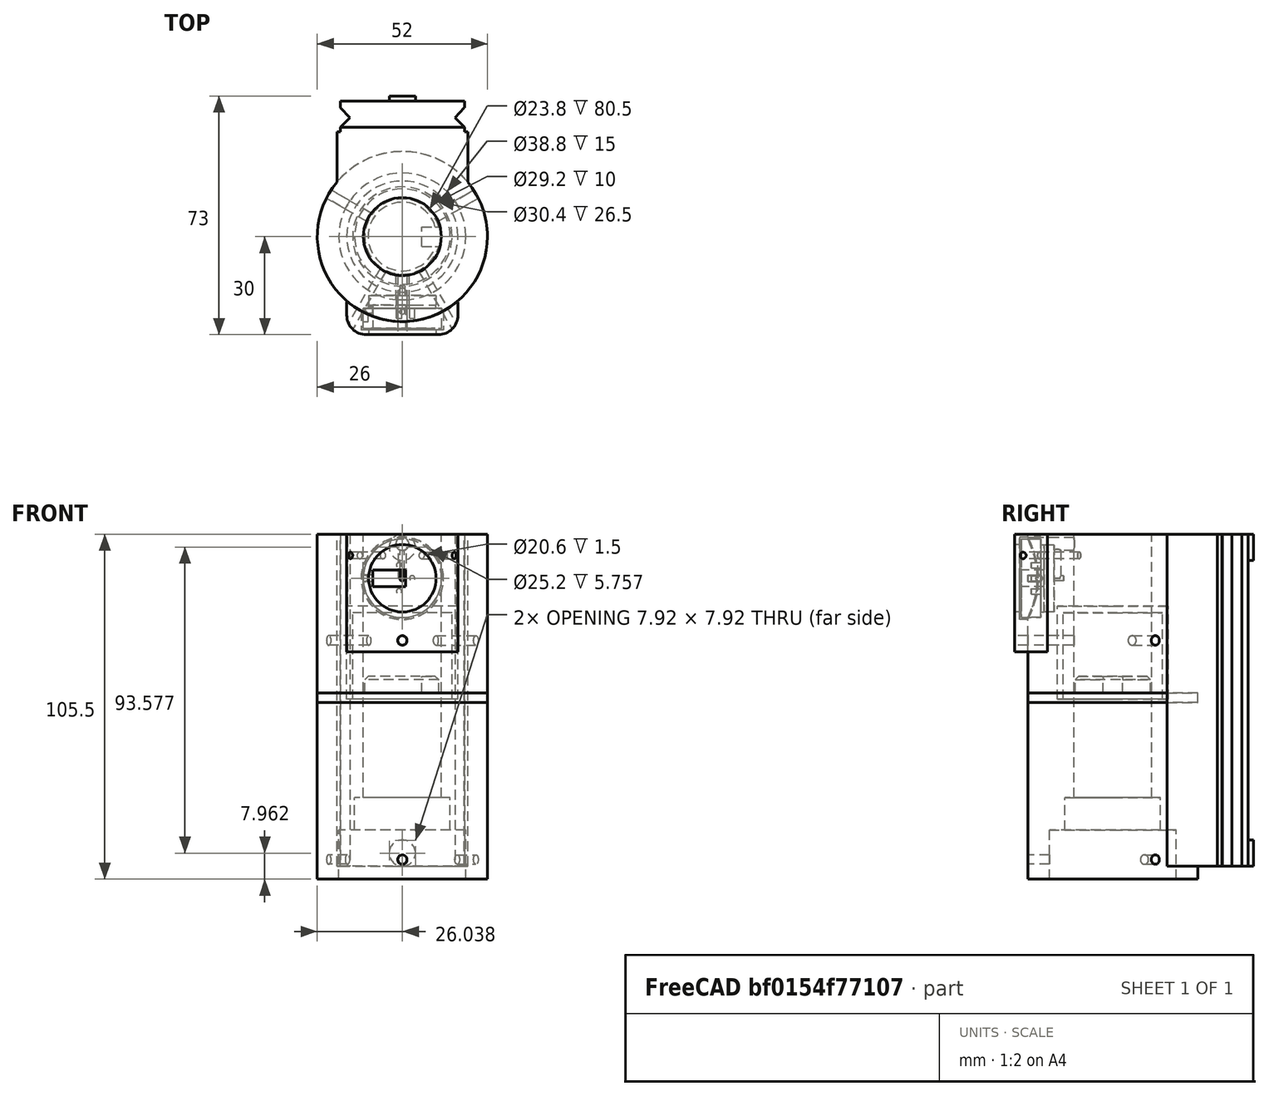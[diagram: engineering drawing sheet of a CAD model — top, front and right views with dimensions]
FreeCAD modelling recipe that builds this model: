
FCSTD DOCUMENT  (FreeCAD 0.17R13387 (Git))
Label: polar scope
License: All rights reserved
LicenseURL: http://en.wikipedia.org/wiki/All_rights_reserved
objects: Part::Cylinder×31, Part::MultiFuse×15, Part::Cut×11, Part::Feature×10, Part::Box×8, Part::Chamfer×2, Part::Fillet×1, App::Part×1
note: 78 computed .brp shape members not serialized (recipe doc carries the construction recipe); baked Part::Feature solids carry a one-line shape summary decoded from their .brp

FEATURE [Part::Feature] Chamfer008019  label="Zaklad009"
  shape: bbox 61 x 63.5 x 101.5 mm, 101 faces (baked)
FEATURE [Part::Cylinder] Cylinder014005804  label="Válec717"
  Angle = 360
  AttacherType = Attacher::AttachEngine3D
  Height = 25
  Placement = pos=(0,0,-51) rot=(0,0,1;0rad)
  Radius = 14.6
FEATURE [Part::Cylinder] Cylinder014005805  label="Válec718"
  Angle = 360
  AttacherType = Attacher::AttachEngine3D
  Height = 40
  Placement = pos=(-40,1,-17.5) rot=(0,1,0;1.5708rad)
  Radius = 0.01
FEATURE [Part::Box] Box207  label="Krychle182"
  AttacherType = Attacher::AttachEngine3D
  Height = 13
  Length = 0.01
  Placement = pos=(-32,-4.5,-55) rot=(0,0,1;0rad)
  Width = 28
FEATURE [Part::Cylinder] Cylinder014005807  label="Válec720"
  Angle = 360
  AttacherType = Attacher::AttachEngine3D
  Height = 74
  Placement = pos=(-40,0,-46.5) rot=(0,1,0;1.5708rad)
  Radius = 0.01
FEATURE [Part::Cylinder] Cylinder014005808  label="Válec721"
  Angle = 360
  AttacherType = Attacher::AttachEngine3D
  Height = 40
  Placement = pos=(-40,16,-17.5) rot=(0,1,0;1.5708rad)
  Radius = 0.01
FEATURE [Part::Box] Box205  label="Krychle180"
  AttacherType = Attacher::AttachEngine3D
  Height = 101.5
  Length = 51
  Placement = pos=(-25.5,-22.5,-51) rot=(0,0,1;0rad)
  Width = 44
FEATURE [Part::Chamfer] Chamfer008018
  Base = -> Box205
  Edges = 2 edges r=7: [Edge1,Edge5]
FEATURE [Part::Box] Box206  label="Krychle181"
  AttacherType = Attacher::AttachEngine3D
  Height = 13
  Length = 0.01
  Placement = pos=(30,-4.5,-55) rot=(0,0,1;0rad)
  Width = 28
FEATURE [Part::Cylinder] Cylinder014005806  label="Válec719"
  Angle = 360
  AttacherType = Attacher::AttachEngine3D
  Height = 74
  Placement = pos=(-40,19,-46.5) rot=(0,1,0;1.5708rad)
  Radius = 0.01
FEATURE [Part::Cylinder] Cylinder014005809  label="Válec722"
  Angle = 360
  AttacherType = Attacher::AttachEngine3D
  Height = 105.5
  Placement = pos=(0,0,-51) rot=(0,0,1;0rad)
  Radius = 11.9
FEATURE [Part::MultiFuse] Fusion001089083
  Shapes = -> [Box206,Box207]
FEATURE [Part::MultiFuse] Fusion001089082
  Shapes = -> [Cylinder014005807,Cylinder014005806]
FEATURE [Part::MultiFuse] Fusion001089078
  Shapes = -> [Fusion001089083,Fusion001089082]
FEATURE [Part::Cut] Cut061098124  label="Zaklad 004"
  Base = -> Chamfer008019
  Tool = -> Fusion001089078
FEATURE [Part::MultiFuse] Fusion001089079
  Shapes = -> [Cylinder014005805,Cylinder014005808]
FEATURE [Part::Cut] Cut061098123  label="RA Zaklad004"
  Base = -> Cut061098124
  Tool = -> Fusion001089079
FEATURE [Part::MultiFuse] Fusion001089081  label="BASE"
  Shapes = -> [Cut061098123,Chamfer008018]
FEATURE [Part::Cylinder] Cylinder014005812  label="Válec725"
  Angle = 360
  AttacherType = Attacher::AttachEngine3D
  Height = 15
  Placement = pos=(0,0,-51) rot=(0,0,1;0rad)
  Radius = 19.4
FEATURE [Part::Cylinder] Cylinder014005813  label="Válec726"
  Angle = 360
  AttacherType = Attacher::AttachEngine3D
  Height = 105.5
  Placement = pos=(0,0,-55) rot=(1,0,0;0rad)
  Radius = 26
FEATURE [Part::Box] Box  label="Krychle"
  AttacherType = Attacher::AttachEngine3D
  Height = 101.5
  Length = 64
  Placement = pos=(-32,-32,-51) rot=(0,0,1;0rad)
  Width = 64
FEATURE [Part::Cut] Cut
  Base = -> Fusion001089081
  Tool = -> Box
FEATURE [Part::Box] Box208  label="Krychle183"
  AttacherType = Attacher::AttachEngine3D
  Height = 101.5
  Length = 40
  Placement = pos=(-20,0,-51) rot=(0,0,1;0rad)
  Width = 32
FEATURE [Part::MultiFuse] Fusion
  Shapes = -> [Cylinder014005813,Box208]
FEATURE [Part::MultiFuse] Fusion001089080
  Placement = pos=(0,0,-4) rot=(0,0,1;0rad)
  Shapes = -> [Cylinder014005809,Cylinder014005804,Cylinder014005812]
FEATURE [Part::MultiFuse] Fusion001089084
  Shapes = -> [Cut,Fusion]
FEATURE [Part::Cut] Cut061098125
  Base = -> Fusion001089084
  Tool = -> Fusion001089080
FEATURE [Part::Cylinder] Cylinder  label="bat1"
  Angle = 360
  AttacherType = Attacher::AttachEngine3D
  Height = 8
  Placement = pos=(0,-18,37) rot=(1,0,0;1.5708rad)
  Radius = 10.3
FEATURE [Part::Cylinder] Cylinder014005814  label="Válec727"
  Angle = 360
  AttacherType = Attacher::AttachEngine3D
  Height = 31
  Placement = pos=(0,0,-49) rot=(1,0,0;1.5708rad)
  Radius = 1.44
FEATURE [Part::Feature] Cylinder014005814001  label="Válec728"
  Placement = pos=(0,0,0) rot=(0,0,1;2.0944rad)
  shape: bbox 28.29 x 17.99 x 2.88 mm, 3 faces (baked)
FEATURE [Part::Feature] Cylinder014005814002  label="Válec729"
  Placement = pos=(0,0,0) rot=(0,0,1;4.18879rad)
  shape: bbox 28.29 x 17.99 x 2.88 mm, 3 faces (baked)
FEATURE [Part::Cylinder] Cylinder014005814003  label="led"
  Angle = 360
  AttacherType = Attacher::AttachEngine3D
  Height = 15
  Placement = pos=(0,-11,47.5) rot=(1,0,0;1.5708rad)
  Radius = 2
FEATURE [Part::Cylinder] Cylinder014005814004  label="Válec731"
  Angle = 360
  AttacherType = Attacher::AttachEngine3D
  Height = 31
  Placement = pos=(0,0,18) rot=(1,0,0;1.5708rad)
  Radius = 1.44
FEATURE [Part::Cylinder] Cylinder014005814005  label="bat2"
  Angle = 360
  AttacherType = Attacher::AttachEngine3D
  Height = 4
  Placement = pos=(0,-22,37) rot=(1,0,0;1.5708rad)
  Radius = 12
FEATURE [Part::Feature] Cylinder014005814004001  label="Válec732"
  Placement = pos=(0,0,0) rot=(0,0,1;2.0944rad)
  shape: bbox 28.29 x 17.99 x 2.88 mm, 3 faces (baked)
FEATURE [Part::Feature] Cylinder014005814004002  label="Válec733"
  Placement = pos=(0,0,0) rot=(0,0,1;4.18879rad)
  shape: bbox 28.29 x 17.99 x 2.88 mm, 3 faces (baked)
FEATURE [Part::Cylinder] Cylinder014005814004003  label="bat003"
  Angle = 360
  AttacherType = Attacher::AttachEngine3D
  Height = 3
  Placement = pos=(0,-15,37) rot=(1,0,0;1.5708rad)
  Radius = 0.8
FEATURE [Part::Cylinder] Cylinder014005814004004  label="Válec"
  Angle = 360
  AttacherType = Attacher::AttachEngine3D
  Height = 11
  Placement = pos=(0,-17,37) rot=(0,0,1;0rad)
  Radius = 1.2
FEATURE [Part::Cylinder] Cylinder014005814004005  label="Válec734"
  Angle = 360
  AttacherType = Attacher::AttachEngine3D
  Height = 2
  Placement = pos=(0,-23,48) rot=(0,0,1;0rad)
  Radius = 0.8
FEATURE [Part::MultiFuse] Fusion001089085
  Shapes = -> [Cylinder,Cylinder014005814,Cylinder014005814001,Cylinder014005814002,Cylinder014005814003,Cylinder014005814004,Cylinder014005814005,Cylinder014005814004001,Cylinder014005814004002,Cylinder014005814004003,Cylinder014005814004004,Cylinder014005814004005]
FEATURE [Part::Cut] Cut061098126  label="PolarScope"
  Base = -> Cut061098125
  Tool = -> Fusion001089085
FEATURE [Part::Cylinder] Cylinder014005814004007  label="bat004"
  Angle = 360
  AttacherType = Attacher::AttachEngine3D
  Height = 6
  Placement = pos=(0,0,0) rot=(1,0,0;1.5708rad)
  Radius = 12
FEATURE [Part::Cylinder] Cylinder014005814004008  label="bat005"
  Angle = 360
  AttacherType = Attacher::AttachEngine3D
  Height = 7
  Placement = pos=(0,0,0) rot=(1,0,0;1.5708rad)
  Radius = 10.3
FEATURE [Part::Box] Box209  label="Krychle184"
  AttacherType = Attacher::AttachEngine3D
  Height = 5
  Length = 10
  Placement = pos=(-1,-7,-2.5) rot=(0,0,1;0rad)
  Width = 11
FEATURE [Part::Cylinder] Cylinder014005814004009  label="Válec735"
  Angle = 360
  AttacherType = Attacher::AttachEngine3D
  Height = 12
  Placement = pos=(0,-5.5,0) rot=(0,1,0;1.5708rad)
  Radius = 1
FEATURE [Part::MultiFuse] Fusion001089086
  Shapes = -> [Cylinder014005814004007,Cylinder014005814004008]
FEATURE [Part::Cylinder] Cylinder014005814004010  label="Válec736"
  Angle = 360
  AttacherType = Attacher::AttachEngine3D
  Height = 4
  Placement = pos=(11.5,-2,0) rot=(1,0,0;1.5708rad)
  Radius = 1
FEATURE [Part::Cylinder] Cylinder014005814004011  label="Válec737"
  Angle = 360
  AttacherType = Attacher::AttachEngine3D
  Height = 4
  Placement = pos=(-3,-3,0) rot=(1,0,0;1.5708rad)
  Radius = 0.8
FEATURE [Part::Cylinder] Cylinder014005814004012  label="Válec738"
  Angle = 360
  AttacherType = Attacher::AttachEngine3D
  Height = 4
  Placement = pos=(1,-3,4) rot=(1,0,0;1.5708rad)
  Radius = 0.8
FEATURE [Part::Cylinder] Cylinder014005814004013  label="Válec739"
  Angle = 360
  AttacherType = Attacher::AttachEngine3D
  Height = 4
  Placement = pos=(1,-3,-4) rot=(1,0,0;1.5708rad)
  Radius = 0.8
FEATURE [Part::MultiFuse] Fusion001089087
  Shapes = -> [Box209,Cylinder014005814004009,Cylinder014005814004010,Cylinder014005814004011,Cylinder014005814004012,Cylinder014005814004013]
FEATURE [Part::Cut] Cut061098127  label="BeterryKnob"
  Base = -> Fusion001089086
  Placement = pos=(0,-28,37) rot=(0,0,1;3.14159rad)
  Tool = -> Fusion001089087
FEATURE [Part::Box] Box210  label="Krychle185"
  AttacherType = Attacher::AttachEngine3D
  Height = 36
  Length = 34
  Placement = pos=(-17,-30,14.5) rot=(0,0,1;0rad)
  Width = 10
FEATURE [Part::Feature] Cut061098126001  label="PlarFinder001"
  shape: bbox 52 x 69 x 105.5 mm, 52 faces (baked)
FEATURE [Part::Cylinder] Cylinder014005814004014  label="bat006"
  Angle = 360
  AttacherType = Attacher::AttachEngine3D
  Height = 11.5
  Placement = pos=(0,-17,37) rot=(1,0,0;1.5708rad)
  Radius = 12.6
FEATURE [Part::Cylinder] Cylinder014005814004015  label="bat007"
  Angle = 360
  AttacherType = Attacher::AttachEngine3D
  Height = 14
  Placement = pos=(0,-18,37) rot=(1,0,0;1.5708rad)
  Radius = 10.3
FEATURE [Part::Cylinder] Cylinder014005814004016  label="Válec740"
  Angle = 360
  AttacherType = Attacher::AttachEngine3D
  Height = 31
  Placement = pos=(0,0,18) rot=(1,0,0;1.5708rad)
  Radius = 1.44
FEATURE [Part::Cylinder] Cylinder014005814004017  label="Válec741"
  Angle = 360
  AttacherType = Attacher::AttachEngine3D
  Height = 2
  Placement = pos=(0,-23,48) rot=(0,0,1;0rad)
  Radius = 0.8
FEATURE [Part::MultiFuse] Fusion001089088
  Shapes = -> [Cut061098126001,Cylinder014005814004014,Cylinder014005814004015,Cylinder014005814004016,Cylinder014005814004017]
FEATURE [Part::Cut] Cut061098126002
  Base = -> Box210
  Tool = -> Fusion001089088
FEATURE [Part::Fillet] Fillet
  Base = -> Cut061098126002
  Edges = 2 edges r=6: [Edge1,Edge6]
FEATURE [Part::Feature] Cylinder014005814004018001  label="Válec743"
  Placement = pos=(0,0,0) rot=(0,0,1;0.523599rad)
  shape: bbox 20.23 x 33.04 x 2 mm, 3 faces (baked)
FEATURE [Part::Feature] Cylinder014005814004018002  label="Válec744"
  Placement = pos=(0,0,0) rot=(0,0,-1;0.523599rad)
  shape: bbox 20.23 x 33.04 x 2 mm, 3 faces (baked)
FEATURE [Part::MultiFuse] Fusion001089089
  Shapes = -> [Cylinder014005814004018001,Cylinder014005814004018002]
FEATURE [Part::Cut] Cut061098126003  label="Cover"
  Base = -> Fillet
  Tool = -> Fusion001089089
FEATURE [Part::Feature] Cylinder014005814004018003  label="Válec745"
  Placement = pos=(0,0,0) rot=(0,0,1;0.523599rad)
  shape: bbox 20.23 x 33.04 x 2 mm, 3 faces (baked)
FEATURE [Part::Feature] Cylinder014005814004018004  label="Válec746"
  Placement = pos=(0,0,0) rot=(0,0,-1;0.523599rad)
  shape: bbox 20.23 x 33.04 x 2 mm, 3 faces (baked)
FEATURE [Part::MultiFuse] Fusion001089090
  Shapes = -> [Cylinder014005814004018003,Cylinder014005814004018004]
FEATURE [Part::Cut] Cut061098126004  label="PolarScope001"
  Base = -> Cut061098126
  Tool = -> Fusion001089090
FEATURE [App::Part] Part
  Group = -> [Cylinder014005814004003,Chamfer008019,Cylinder014005814001,Fusion001089078,Cylinder014005814,Cylinder,Cylinder014005814003,Cylinder014005814004,Cylinder014005814005,Cut061098126,Cut,Cut061098124,Cut061098125,Cut061098123,Chamfer008018,Cylinder014005808,Box205,Cylinder014005812,Box206,Cylinder014005804,Cylinder014005813,Box208,Cylinder014005806,Box207,Cylinder014005807,Cylinder014005805,+43 more]
  License = CC BY 3.0
  LicenseURL = http://creativecommons.org/licenses/by/3.0/
  Origin = -> Origin
FEATURE [Part::Cylinder] Cylinder001  label="Válec001"
  Angle = 360
  AttacherType = Attacher::AttachEngine3D
  Height = 26.5
  Radius = 15.2
FEATURE [Part::Cylinder] Cylinder014005814004018005  label="Válec747"
  Angle = 360
  AttacherType = Attacher::AttachEngine3D
  Height = 28.5
  Radius = 17
FEATURE [Part::Cut] Cut061098126005  label="Cap1"
  Base = -> Cylinder014005814004018005
  Tool = -> Cylinder001
FEATURE [Part::Cylinder] Cylinder014005814004018006  label="Válec748"
  Angle = 360
  AttacherType = Attacher::AttachEngine3D
  Height = 7
  Radius = 11.5
FEATURE [Part::Cylinder] Cylinder014005814004018007  label="Válec749"
  Angle = 360
  AttacherType = Attacher::AttachEngine3D
  Height = 3
  Placement = pos=(0,0,-1) rot=(0,0,1;0rad)
  Radius = 26
FEATURE [Part::Box] Box211  label="Krychle186"
  AttacherType = Attacher::AttachEngine3D
  Height = 5
  Length = 6
  Placement = pos=(6,-3,2) rot=(0,0,1;0rad)
  Width = 6
FEATURE [Part::MultiFuse] Fusion001089091
  Shapes = -> [Cylinder014005814004018006,Cylinder014005814004018007]
FEATURE [Part::Cut] Cut061098126006
  Base = -> Fusion001089091
  Tool = -> Box211
FEATURE [Part::Chamfer] Chamfer  label="Cap2"
  Base = -> Cut061098126006
  Edges = 1 edges r=1: [Edge4]
